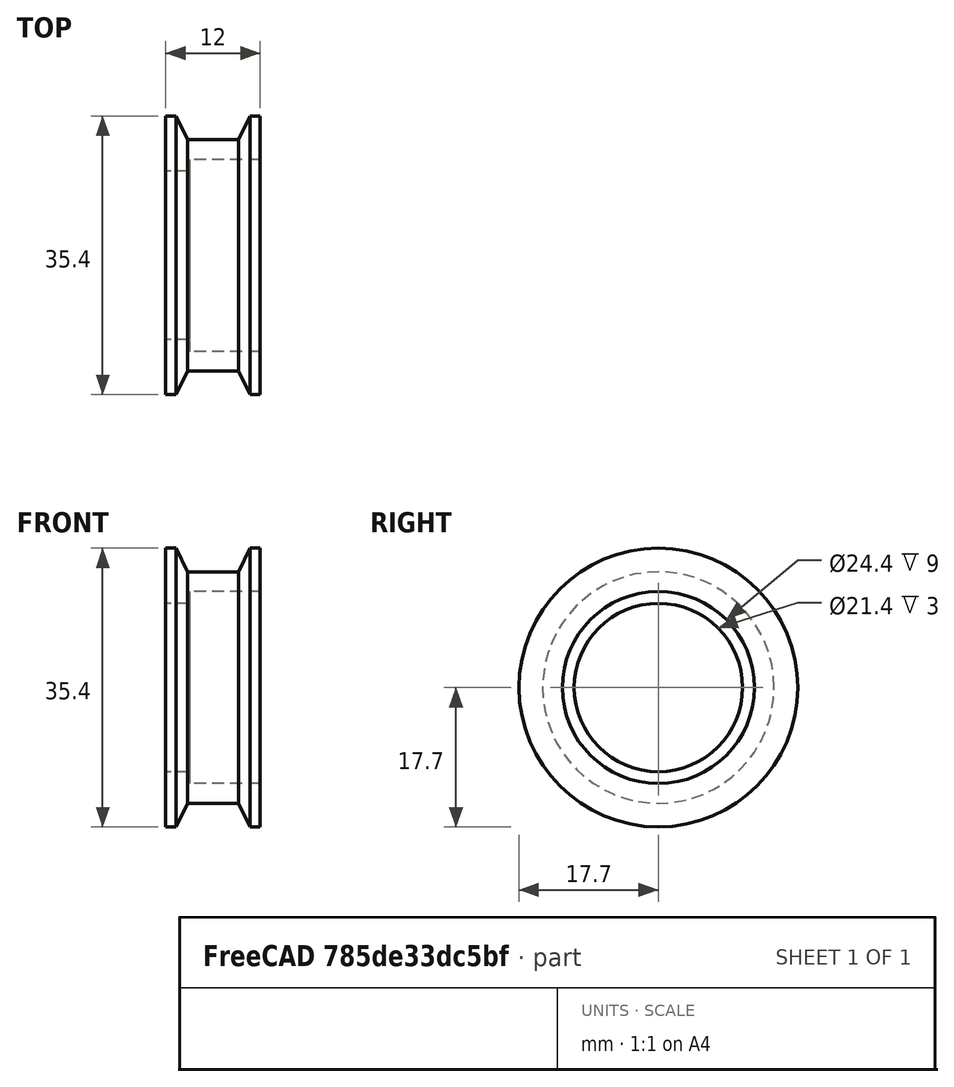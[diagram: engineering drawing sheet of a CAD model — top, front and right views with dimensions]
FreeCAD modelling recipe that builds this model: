
FCSTD DOCUMENT  (FreeCAD 0.17R13522 (Git))
Label: AnelRolamento
License: All rights reserved
LicenseURL: http://en.wikipedia.org/wiki/All_rights_reserved
objects: Sketcher::SketchObject×1, PartDesign::Revolution×1, PartDesign::Body×1
note: 4 computed .brp shape members not serialized (recipe doc carries the construction recipe); baked Part::Feature solids carry a one-line shape summary decoded from their .brp

FEATURE [Sketcher::SketchObject] Sketch
  MapMode = 5
  Support = -> [XY_Plane]
  sketch-geometry (11):
    g0: LineSegment StartX=-6 StartY=12.2 StartZ=0 EndX=-6 EndY=17.7 EndZ=0
    g1: LineSegment StartX=-6 StartY=17.7 StartZ=0 EndX=-4.71774 EndY=17.7 EndZ=0
    g2: LineSegment StartX=4.71774 StartY=17.7 StartZ=0 EndX=6 EndY=17.7 EndZ=0
    g3: LineSegment StartX=6 StartY=17.7 StartZ=0 EndX=6 EndY=12.2 EndZ=0
    g4: LineSegment StartX=6 StartY=12.2 StartZ=0 EndX=-3 EndY=12.2 EndZ=0
    g5: LineSegment StartX=-4.71774 StartY=17.7 StartZ=0 EndX=-3.25 EndY=14.7 EndZ=0
    g6: LineSegment StartX=-3.25 StartY=14.7 StartZ=0 EndX=3.25 EndY=14.7 EndZ=0
    g7: LineSegment StartX=3.25 StartY=14.7 StartZ=0 EndX=4.71774 EndY=17.7 EndZ=0
    g8: LineSegment StartX=-3 StartY=12.2 StartZ=0 EndX=-3 EndY=10.7 EndZ=0
    g9: LineSegment StartX=-3 StartY=10.7 StartZ=0 EndX=-6 EndY=10.7 EndZ=0
    g10: LineSegment StartX=-6 StartY=10.7 StartZ=0 EndX=-6 EndY=12.2 EndZ=0
  constraints (35):
    c: Coincident(g0,g1)
    c: Coincident(g2,g3)
    c: Coincident(g3,g4)
    c: Horizontal(g4)
    c: Horizontal(g1)
    c: Horizontal(g2)
    c: Vertical(g0)
    c: Vertical(g3)
    c: DistanceY(g-1,g0) = 12.2
    c: Symmetric(g0,g3,g-2)
    c: DistanceX(g0,g4) = 12
    c: Equal(g3,g0)
    c: Coincident(g5,g6)
    c: Coincident(g6,g7)
    c: Coincident(g2,g7)
    c: Coincident(g1,g5)
    c: Horizontal(g6)
    c: DistanceX(g6,g6) = 6.5
    c: Symmetric(g5,g6,g-2)
    c: Equal(g1,g2)
    c: DistanceY(g6,g2) = 3
    c: DistanceY(g3,g6) = 2.5
    c: DistanceY(g0,g0) = 5.5
    c: DistanceY(g-1,g2) = 17.7
    c: Coincident(g8,g9)
    c: Coincident(g9,g10)
    c: Horizontal(g9)
    c: Vertical(g8)
    c: Vertical(g10)
    c: DistanceX(g9,g9) = 3
    c: DistanceY(g10,g10) = 1.5
    c: Equal(g10,g8)
    c: Coincident(g0,g10)
    c: PointOnObject(g4,g8)
    c: DistanceY(g-1,g8) = 10.7
FEATURE [PartDesign::Revolution] Revolution
  Angle = 360
  Axis = (1,0,0)
  Base = (0,0,0)
  Profile = -> Sketch
  ReferenceAxis = -> Sketch [H_Axis]
FEATURE [PartDesign::Body] Body
  Group = -> [Sketch,Revolution]
  Origin = -> Origin
  Tip = -> Revolution
